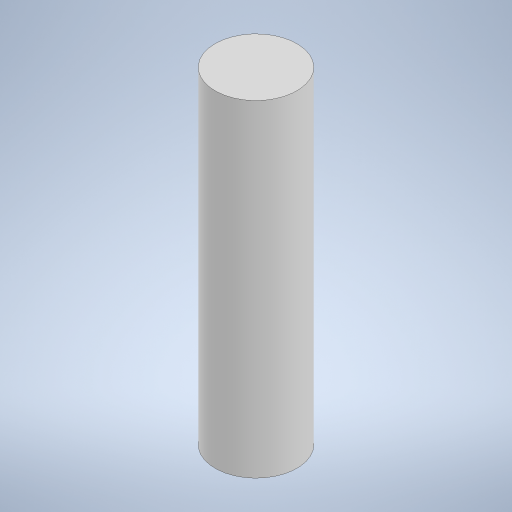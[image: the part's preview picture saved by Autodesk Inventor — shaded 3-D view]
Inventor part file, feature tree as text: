
AUTODESK INVENTOR PART (.ipt)
format: ipt  version: 2023 (Build 270158000, 158)  size: 212,480 bytes
history: native  units: mm
features: other x1, extrude x1, sketch x1
ambient origin geometry x8: Origin, YZ Plane, XZ Plane, XY Plane, X Axis, Y Axis, Z Axis, Center Point
bodies: Body1 (feature_tree)
feature tree (3):
  other  "Sólido1"
  extrude  "Extrusión1"  Depth=40.0mm TaperAngle=0.0deg
  sketch  "Boceto1"  dims[d0=10.0mm d1=40.0mm d2=0.0mm]
